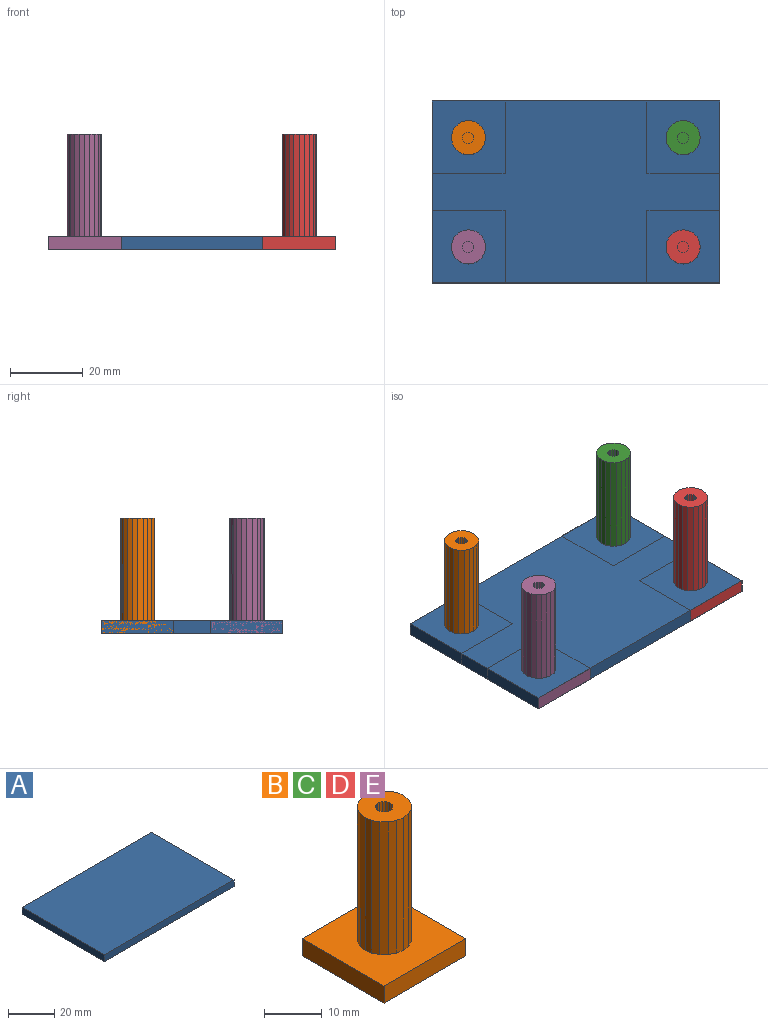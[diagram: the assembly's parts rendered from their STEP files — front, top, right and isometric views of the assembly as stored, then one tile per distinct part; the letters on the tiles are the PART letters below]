
ASSEMBLY  parts=5 mates=4
PART A: 6 faces, bbox 79x50x3.6 mm
  f0: plane 50x3.64mm, normal (-1,0,0), area 181.9mm2, adj f1,f3,f4,f5
  f1: plane 79x3.64mm, normal (0,-1,0), area 287.3mm2, adj f0,f2,f4,f5
  f2: plane 50x3.64mm, normal (1,0,0), area 181.9mm2, adj f1,f3,f4,f5
  f3: plane 79x3.64mm, normal (0,1,0), area 287.3mm2, adj f0,f2,f4,f5
  f4: plane 79x50mm, normal (0,0,1), area 3950mm2, adj f0,f1,f2,f3
  f5: plane 79x50mm, normal (0,0,-1), area 3950mm2, adj f0,f1,f2,f3
PART B: 50 faces, bbox 20x20x31.8 mm
  f0: plane 20x20mm, normal (0,0,-1), area 400mm2, adj f1,f18,f21,f29
  f1: plane 20x3.64mm, normal (-1,0,0), area 72.7mm2, adj f0,f9,f18,f29
  f2: plane 28.11x1.04mm, normal (0.71,0.71,0), area 41.3mm2, adj f3,f9,f22,f23
  f3: plane 9.4x9.4mm, normal (0,0,1), area 60.8mm2, adj f2,f5,f7,f8,f10,f11,f13,f14
  f4: plane 28.11x1.13mm, normal (-0.45,0.89,0), area 17.7mm2, adj f5,f9,f34
  f5: plane 28.11x1.31mm, normal (-0.45,0.89,0), area 20.7mm2, adj f3,f4,f6
  f6: plane 28.11x0.19mm, normal (-0.45,0.89,0), area 2.9mm2, adj f5,f9,f27
  f7: plane 28.11x1.31mm, normal (0.45,-0.89,0), area 41.3mm2, adj f3,f8,f9,f37
  f8: plane 28.11x1.04mm, normal (0.71,-0.71,0), area 41.3mm2, adj f3,f7,f9,f24
  f9: plane 20x20mm, normal (0,0,1), area 331.7mm2, adj f1,f2,f4,f6,f7,f8,f14,f15
  f10: plane 27.66x0.43mm, normal (-0.45,-0.89,0), area 13.4mm2, adj f3,f11,f12,f49
  f11: plane 27.66x0.34mm, normal (-0.71,-0.71,0), area 13.4mm2, adj f3,f10,f12,f38
  f12: plane 3.11x3.11mm, normal (0,0,1), area 7.4mm2, adj f10,f11,f13,f30,f31,f32,f33,f35
  f13: plane 27.66x0.43mm, normal (0.89,0.45,0), area 13.4mm2, adj f3,f12,f33,f35
  f14: plane 28.11x1.31mm, normal (-0.89,-0.45,0), area 41.3mm2, adj f3,f9,f17,f20
  f15: plane 28.11x1.45mm, normal (-0.99,0.16,0), area 41.4mm2, adj f3,f9,f19,f20
  f16: plane 28.11x1.31mm, normal (-0.45,-0.89,0), area 41.3mm2, adj f3,f9,f17,f39
  f17: plane 28.11x1.04mm, normal (-0.71,-0.71,0), area 41.3mm2, adj f3,f9,f14,f16
  f18: plane 20x3.64mm, normal (0,-1,0), area 72.7mm2, adj f0,f1,f9,f21
  f19: plane 28.11x1.31mm, normal (-0.89,0.45,0), area 41.3mm2, adj f3,f9,f15,f34
  f20: plane 28.11x1.45mm, normal (-0.99,-0.16,0), area 41.3mm2, adj f3,f9,f14,f15
  f21: plane 20x3.64mm, normal (1,0,0), area 72.7mm2, adj f0,f9,f18,f29
  f22: plane 28.11x1.31mm, normal (0.89,0.45,0), area 41.3mm2, adj f2,f3,f9,f26
  f23: plane 28.11x1.31mm, normal (0.45,0.89,0), area 41.3mm2, adj f2,f3,f9,f28
  f24: plane 28.11x1.31mm, normal (0.89,-0.45,0), area 41.3mm2, adj f3,f8,f9,f25
  f25: plane 28.11x1.45mm, normal (0.99,-0.16,0), area 41.3mm2, adj f3,f9,f24,f26
  f26: plane 28.11x1.45mm, normal (0.99,0.16,0), area 41.4mm2, adj f3,f9,f22,f25
  f27: plane 28.11x1.45mm, normal (-0.16,0.99,0), area 41.3mm2, adj f3,f6,f9,f28
  f28: plane 28.11x1.45mm, normal (0.16,0.99,0), area 41.4mm2, adj f3,f9,f23,f27
  f29: plane 20x3.64mm, normal (0,1,0), area 72.7mm2, adj f0,f1,f9,f21
  f30: plane 27.66x0.48mm, normal (0.16,0.99,0), area 13.4mm2, adj f3,f12,f31,f32
  f31: plane 27.66x0.43mm, normal (0.45,0.89,0), area 13.4mm2, adj f3,f12,f30,f33
  f32: plane 27.66x0.48mm, normal (-0.16,0.99,0), area 13.4mm2, adj f3,f12,f30,f46
  f33: plane 27.66x0.34mm, normal (0.71,0.71,0), area 13.4mm2, adj f3,f12,f13,f31
  f34: plane 28.11x1.04mm, normal (-0.71,0.71,0), area 41.3mm2, adj f3,f4,f9,f19
  f35: plane 27.66x0.48mm, normal (0.99,0.16,0), area 13.4mm2, adj f3,f12,f13,f36
  f36: plane 27.66x0.48mm, normal (0.99,-0.16,0), area 13.4mm2, adj f3,f12,f35,f43
  f37: plane 28.11x1.45mm, normal (0.16,-0.99,0), area 41.4mm2, adj f3,f7,f9,f39
  f38: plane 27.66x0.43mm, normal (-0.89,-0.46,0), area 13.4mm2, adj f3,f11,f12,f40
  f39: plane 28.11x1.45mm, normal (-0.16,-0.99,0), area 41.3mm2, adj f3,f9,f16,f37
  f40: plane 27.66x0.48mm, normal (-0.99,-0.16,0), area 13.4mm2, adj f3,f12,f38,f42
  f41: plane 27.66x0.34mm, normal (0.71,-0.71,0), area 13.5mm2, adj f3,f12,f43,f47
  f42: plane 27.66x0.48mm, normal (-0.99,0.16,0), area 13.4mm2, adj f3,f12,f40,f44
  f43: plane 27.66x0.43mm, normal (0.89,-0.45,0), area 13.4mm2, adj f3,f12,f36,f41
  f44: plane 27.66x0.43mm, normal (-0.89,0.45,0), area 13.4mm2, adj f3,f12,f42,f45
  f45: plane 27.66x0.34mm, normal (-0.71,0.71,0), area 13.4mm2, adj f3,f12,f44,f46
  f46: plane 27.66x0.43mm, normal (-0.45,0.89,0), area 13.4mm2, adj f3,f12,f32,f45
  f47: plane 27.66x0.43mm, normal (0.45,-0.89,0), area 13.4mm2, adj f3,f12,f41,f48
  f48: plane 27.66x0.48mm, normal (0.16,-0.99,0), area 13.4mm2, adj f3,f12,f47,f49
  f49: plane 27.66x0.48mm, normal (-0.16,-0.99,0), area 13.4mm2, adj f3,f10,f12,f48
PART C: same geometry as B
PART D: same geometry as B
PART E: same geometry as B
PLACE A t=(-10,-10,0)mm
PLACE B t=(20,43,0)mm
PLACE C t=(79,43,0)mm
PLACE D t=(79,13,0)mm
PLACE E t=(20,13,0)mm
MATE fastened B.f0 <-> E.f0  axis (0,0,-1) through (0,30,0)mm
MATE fastened D.f0 <-> C.f0  axis (0,0,-1) through (59,0,0)mm
MATE fastened E.f0 <-> D.f0  axis (0,0,-1) through (0,0,0)mm
MATE fastened A.f4 <-> B.f9  axis (0,0,1) through (-10,40,3.64)mm
